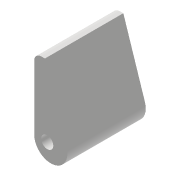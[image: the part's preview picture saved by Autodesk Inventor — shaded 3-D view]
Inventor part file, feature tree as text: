
AUTODESK INVENTOR PART (.ipt)
format: ipt  version: 2022 (Build 260153000, 153)  size: 116,224 bytes
history: native  units: mm
features: sketch x4, extrude x3, other x2, fillet x1, plane x1, reference x1, projected_geometry x1
ambient origin geometry x8: Origin, YZ Plane, XZ Plane, XY Plane, X Axis, Y Axis, Z Axis, Center Point
bodies: Volumenkörper1 (feature_tree)
feature tree (13):
  extrude  "Extrusion1"  Depth=3.0mm
  fillet  "Rundung1"  Radius=1.0mm
  extrude  "Extrusion2"  Depth=22.0mm TaperAngle=0.0deg
  extrude  "Extrusion3"  Depth=2.0mm
  plane  "Arbeitsebene1"
  sketch  "Skizze4"  dims[d8=2.9mm d9=4.0mm d10=0.0mm d11=4.0mm d12=0.0mm d13=2.9mm]
  sketch  "Skizze1"  dims[d0=20.0mm d1=3.0mm d2=1.0mm]
  reference  "Referenz1"
  sketch  "Skizze2"  dims[d3=2.0mm d4=22.0mm d5=0.0mm]
  projected_geometry  "Projizierte Kontur1"
  sketch  "Skizze3"  dims[d6=0.2mm d7=2.0mm]
  other  "Anglerfish_lunchbox_m12large_flipped_v0.iam"
  other  "Anglerfish_coverslipclamp_top:1"
